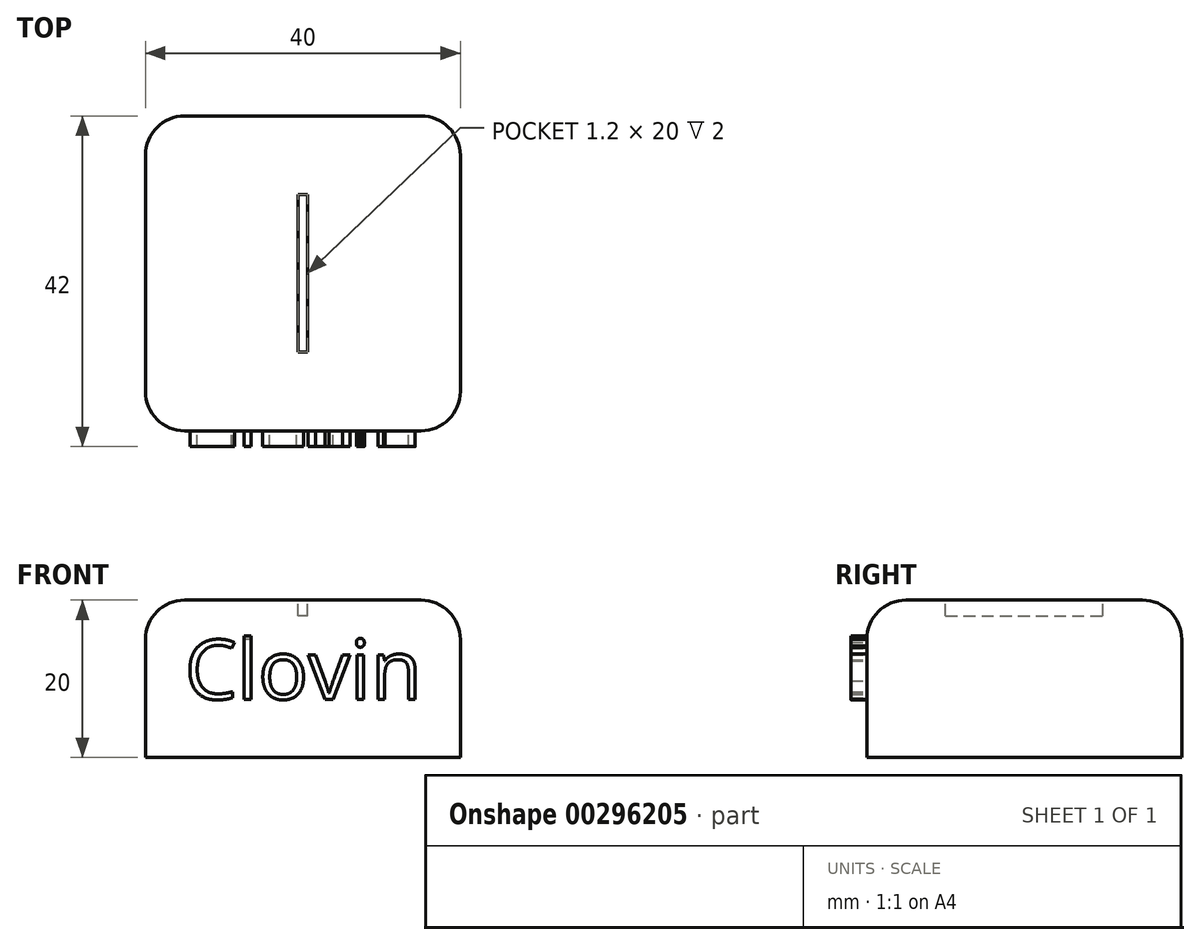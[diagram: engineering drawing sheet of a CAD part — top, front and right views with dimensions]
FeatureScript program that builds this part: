
annotation { "Feature Type Name" : "Feature", "Feature Type Description" : "" }
export const myFeature = defineFeature(function(context is Context, id is Id, definition is map)
    precondition{}
    {
        {
            var Q0;
            Q0=qCreatedBy(makeId("Top.planeOp"),FACE);
            var sketch = newSketch(context, id + "F0", { "sketchPlane" : qUnion([Q0])});
            skLineSegment(sketch, "E0.bottom", {"start": v(20, -20) * mm, "end": v(-20, -20) * mm});
            skLineSegment(sketch, "E0.top", {"start": v(20, 20) * mm, "end": v(-20, 20) * mm});
            skLineSegment(sketch, "E0.left", {"start": v(20, -20) * mm, "end": v(20, 20) * mm});
            skLineSegment(sketch, "E0.right", {"start": v(-20, -20) * mm, "end": v(-20, 20) * mm});
            skPoint(sketch, "E0.middle", {"position": v(0, 0) * mm});
            skLineSegment(sketch, "E1.bottom", {"start": v(0.6, -10) * mm, "end": v(-0.6, -10) * mm});
            skLineSegment(sketch, "E1.top", {"start": v(0.6, 10) * mm, "end": v(-0.6, 10) * mm});
            skLineSegment(sketch, "E1.left", {"start": v(0.6, -10) * mm, "end": v(0.6, 10) * mm});
            skLineSegment(sketch, "E1.right", {"start": v(-0.6, -10) * mm, "end": v(-0.6, 10) * mm});
            skSolve(sketch);
        }
        {
            var Q0;
            Q0=makeQuery(id+"F0.imprint","IMPRINT",FACE,{"disambiguationData":[TD([[makeQuery(id+"F0.imprint","IMPRINT",EDGE,{"derivedFrom":sQuery(id+"F0.wireOp",EDGE,"E0.bottom")}),-1.0]])]});
            var Q1;
            Q1=makeQuery(id+"F0.imprint","IMPRINT",FACE,{"disambiguationData":[TD([[makeQuery(id+"F0.imprint","IMPRINT",EDGE,{"derivedFrom":sQuery(id+"F0.wireOp",EDGE,"E1.bottom")}),-1.0]])]});
            extrude(context, id + "F1", {"entities" : qUnion([Q0, Q1]), "oppositeDirection" : true, "depth" : 20 * mm});
        }
        {
            var Q0;
            Q0=makeQuery(id+"F0.imprint","IMPRINT",FACE,{"disambiguationData":[TD([[makeQuery(id+"F0.imprint","IMPRINT",EDGE,{"derivedFrom":sQuery(id+"F0.wireOp",EDGE,"E1.bottom")}),-1.0]])]});
            extrude(context, id + "F2", {"entities" : qUnion([Q0]), "operationType" : NewBodyOperationType.REMOVE, "oppositeDirection" : true, "depth" : 2 * mm});
        }
        {
            var Q0;
            Q0=makeQuery(id+"F2.boolean.opBoolean","COPY",EDGE,{"derivedFrom":makeQuery(id+"F2.opExtrude","CAP_EDGE",EDGE,{"disambiguationData":[OSD([sQuery(id+"F0.wireOp",EDGE,"E1.left")])],"isStart":true})});
            var Q1;
            Q1=makeQuery(id+"F2.boolean.opBoolean","COPY",EDGE,{"derivedFrom":makeQuery(id+"F2.opExtrude","CAP_EDGE",EDGE,{"disambiguationData":[OSD([sQuery(id+"F0.wireOp",EDGE,"E1.right")])],"isStart":true})});
            var Q2;
            Q2=makeQuery(id+"F1.opExtrude","SWEPT_EDGE",EDGE,{"disambiguationData":[OSD([sQuery(id+"F0.wireOp",EDGE,"E0.bottom"),sQuery(id+"F0.wireOp",EDGE,"E0.left")])]});
            var Q3;
            Q3=makeQuery(id+"F1.opExtrude","SWEPT_EDGE",EDGE,{"disambiguationData":[OSD([sQuery(id+"F0.wireOp",EDGE,"E0.top"),sQuery(id+"F0.wireOp",EDGE,"E0.left")])]});
            var Q4;
            Q4=makeQuery(id+"F1.opExtrude","CAP_EDGE",EDGE,{"disambiguationData":[OSD([sQuery(id+"F0.wireOp",EDGE,"E0.left")])],"isStart":true});
            var Q5;
            Q5=makeQuery(id+"F1.opExtrude","SWEPT_EDGE",EDGE,{"disambiguationData":[OSD([sQuery(id+"F0.wireOp",EDGE,"E0.bottom"),sQuery(id+"F0.wireOp",EDGE,"E0.right")])]});
            var Q6;
            Q6=makeQuery(id+"F1.opExtrude","SWEPT_EDGE",EDGE,{"disambiguationData":[OSD([sQuery(id+"F0.wireOp",EDGE,"E0.top"),sQuery(id+"F0.wireOp",EDGE,"E0.right")])]});
            var Q7;
            Q7=makeQuery(id+"F1.opExtrude","CAP_EDGE",EDGE,{"disambiguationData":[OSD([sQuery(id+"F0.wireOp",EDGE,"E0.top")])],"isStart":true});
            var Q8;
            Q8=makeQuery(id+"F1.opExtrude","CAP_EDGE",EDGE,{"disambiguationData":[OSD([sQuery(id+"F0.wireOp",EDGE,"E0.right")])],"isStart":true});
            var Q9;
            Q9=makeQuery(id+"F1.opExtrude","CAP_EDGE",EDGE,{"disambiguationData":[OSD([sQuery(id+"F0.wireOp",EDGE,"E0.bottom")])],"isStart":true});
            fillet(context, id + "F3", {"entities" : qUnion([Q0, Q1, Q2, Q3, Q4, Q5, Q6, Q7, Q8, Q9]), "radius" : 5 * mm, "tangentPropagation" : true, "allowEdgeOverflow" : false});
        }
        {
            var Q0;
            Q0=makeQuery(id+"F1.opExtrude","SWEPT_FACE",FACE,{"disambiguationData":[OSD([sQuery(id+"F0.wireOp",EDGE,"E0.bottom")])]});
            var sketch = newSketch(context, id + "F4", { "sketchPlane" : qUnion([Q0])});
            skText(sketch, "E2", { "text": "Clovin", "fontName": "OpenSans-Regular.ttf"});
            const initialGuessF4  = {"E2": [-0.015, -0.01259, 1, 0, 0.00759]};
            skSetInitialGuess(sketch, initialGuessF4);
            skSolve(sketch);
        }
        {
            var Q0;
            Q0=qSketchRegion(id+"F4",true);
            extrude(context, id + "F5", {"entities" : qUnion([Q0]), "operationType" : NewBodyOperationType.ADD, "depth" : 2 * mm});
        }
    });
